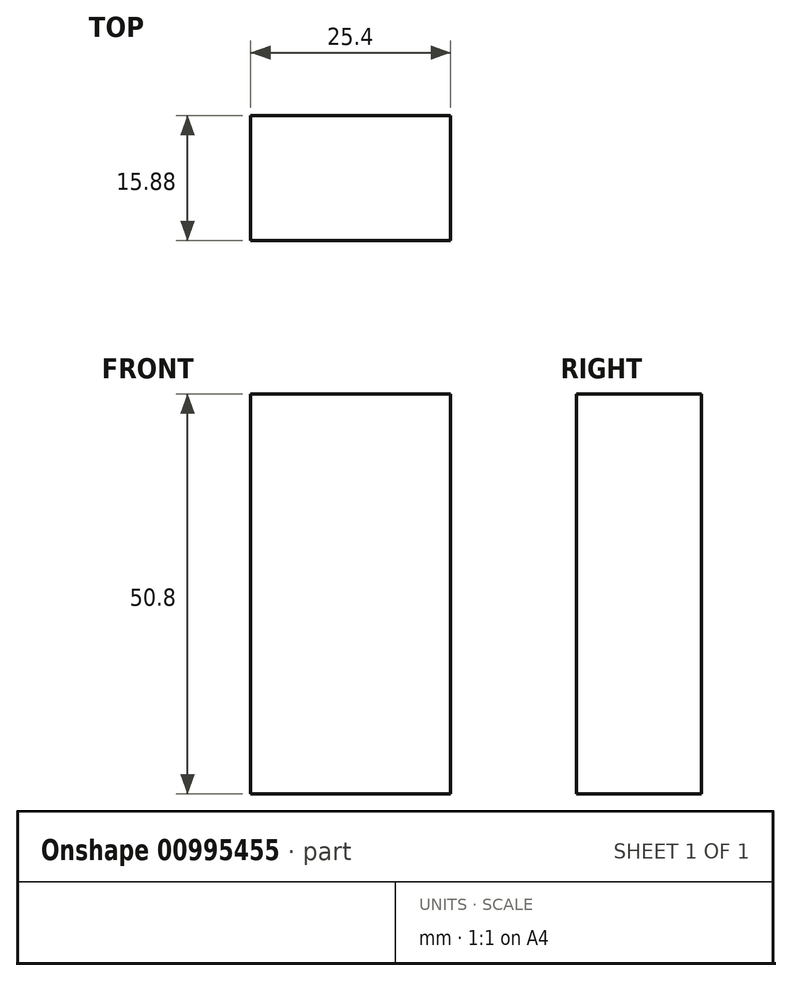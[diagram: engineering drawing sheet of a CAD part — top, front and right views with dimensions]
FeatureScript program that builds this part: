
annotation { "Feature Type Name" : "Feature", "Feature Type Description" : "" }
export const myFeature = defineFeature(function(context is Context, id is Id, definition is map)
    precondition{}
    {
        {
            var Q0;
            Q0=qCreatedBy(makeId("Front.planeOp"),FACE);
            var sketch = newSketch(context, id + "F0", { "sketchPlane" : qUnion([Q0])});
            skLineSegment(sketch, "E0.bottom", {"start": v(0, 0) * mm, "end": v(25.4, 0) * mm});
            skLineSegment(sketch, "E0.top", {"start": v(0, 50.8) * mm, "end": v(25.4, 50.8) * mm});
            skLineSegment(sketch, "E0.left", {"start": v(0, 0) * mm, "end": v(0, 50.8) * mm});
            skLineSegment(sketch, "E0.right", {"start": v(25.4, 0) * mm, "end": v(25.4, 50.8) * mm});
            skSolve(sketch);
        }
        {
            var Q0;
            Q0=makeQuery(id+"F0.imprint","IMPRINT",FACE,{"disambiguationData":[TD([[makeQuery(id+"F0.imprint","IMPRINT",EDGE,{"derivedFrom":sQuery(id+"F0.wireOp",EDGE,"E0.bottom")}),1.0]])]});
            extrude(context, id + "F1", {"entities" : qUnion([Q0]), "oppositeDirection" : true, "depth" : 15.88 * mm, "offsetDistance" : 25.4 * mm});
        }
    });
